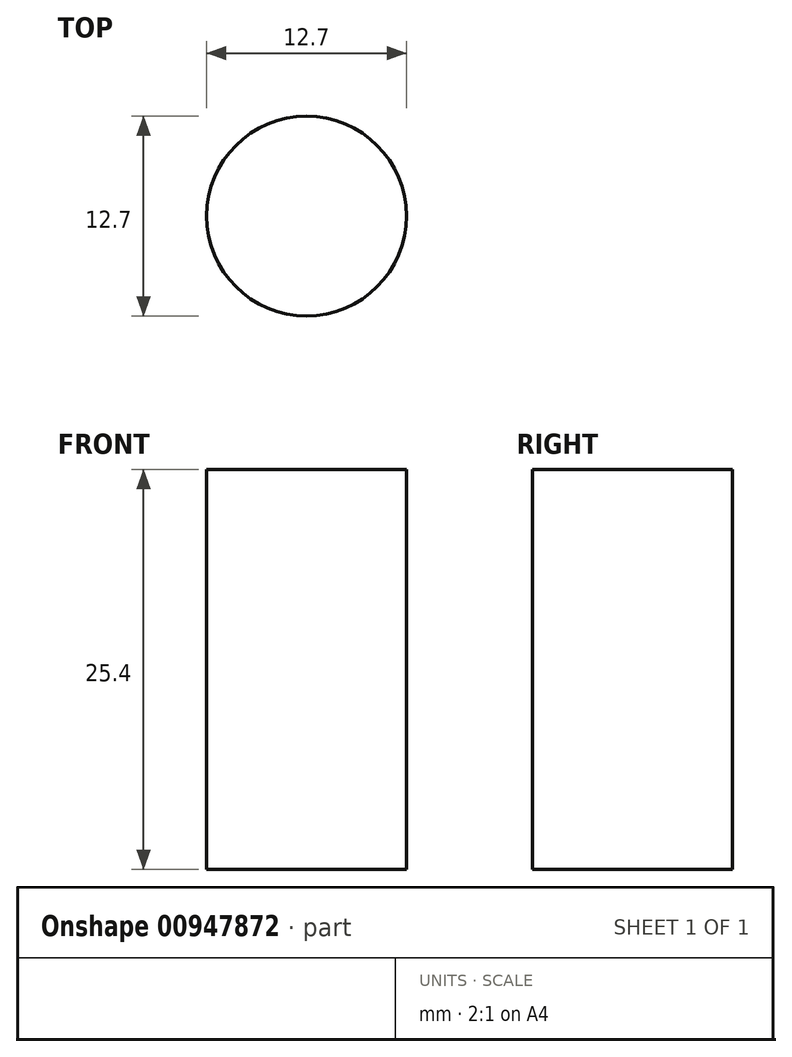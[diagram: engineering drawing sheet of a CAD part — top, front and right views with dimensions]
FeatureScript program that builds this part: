
annotation { "Feature Type Name" : "Feature", "Feature Type Description" : "" }
export const myFeature = defineFeature(function(context is Context, id is Id, definition is map)
    precondition{}
    {
        {
            var Q0;
            Q0=qCreatedBy(makeId("Top.planeOp"),FACE);
            var sketch = newSketch(context, id + "F0", { "sketchPlane" : qUnion([Q0])});
            skCircle(sketch, "E0", {"center": v(0, 0) * mm, "radius": 6.35 * mm});
            skSolve(sketch);
        }
        {
            var Q0;
            Q0 = qSketchRegion(id + "F0", true);
            extrude(context, id + "F1", {"entities" : qUnion([Q0]), "endBound" : BoundingType.SYMMETRIC, "depth" : 25.4 * mm, "offsetDistance" : 25.4 * mm});
        }
    });
